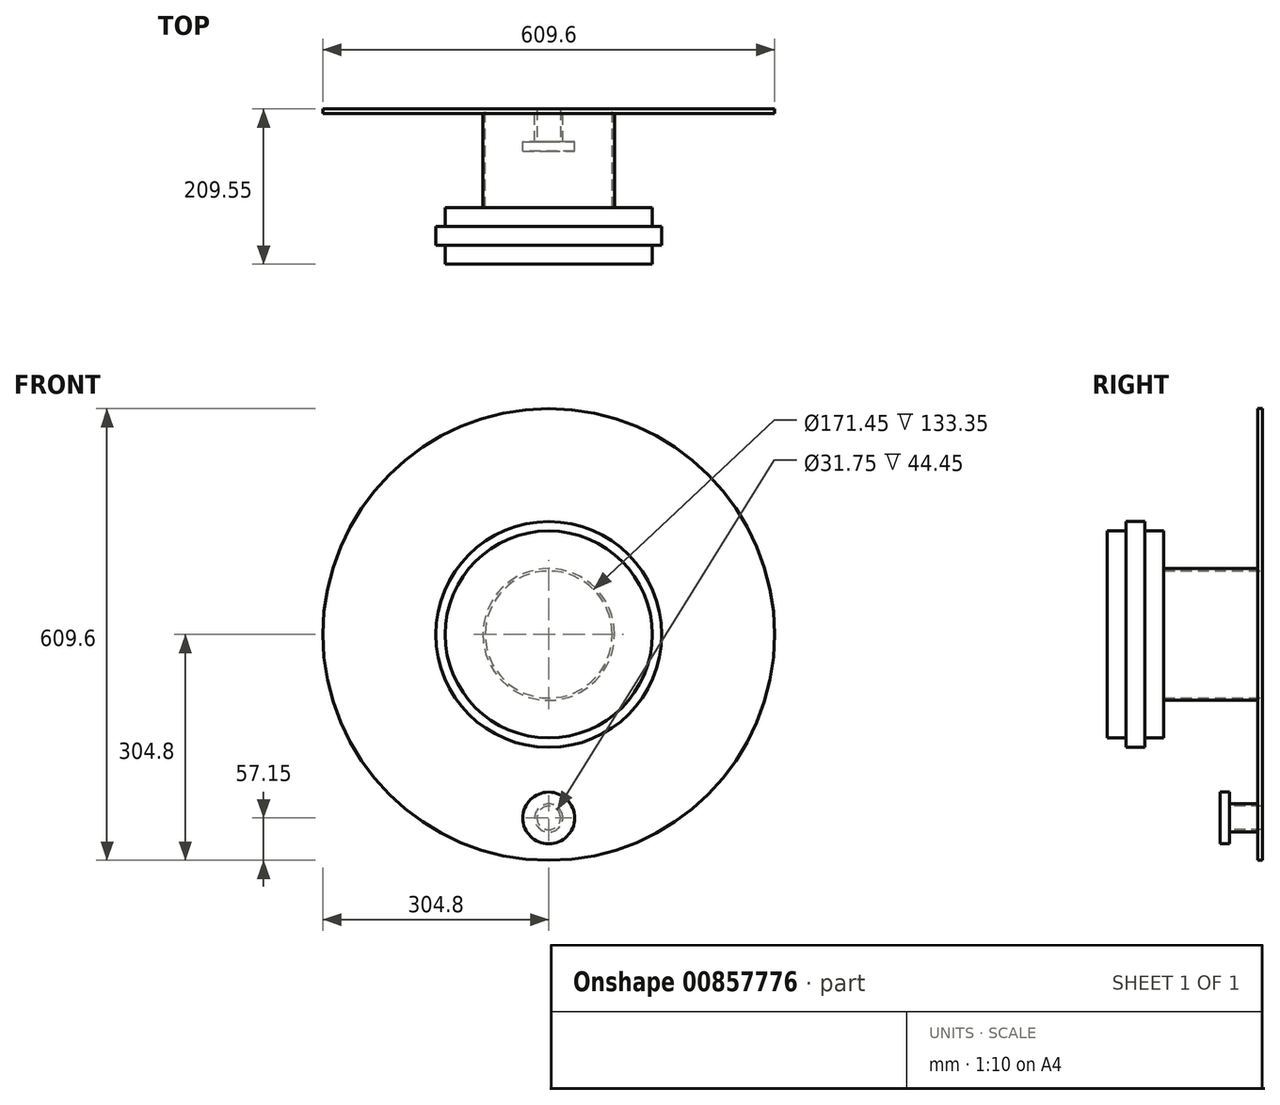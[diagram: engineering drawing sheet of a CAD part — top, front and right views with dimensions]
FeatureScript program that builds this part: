
annotation { "Feature Type Name" : "Feature", "Feature Type Description" : "" }
export const myFeature = defineFeature(function(context is Context, id is Id, definition is map)
    precondition{}
    {
        {
            var Q0;
            Q0=qCreatedBy(makeId("Front.planeOp"),FACE);
            var sketch = newSketch(context, id + "F0", { "sketchPlane" : qUnion([Q0])});
            skCircle(sketch, "E0", {"center": v(0, 0) * mm, "radius": 304.8 * mm});
            skSolve(sketch);
        }
        {
            var Q0;
            Q0=makeQuery(id+"F0.imprint","IMPRINT",FACE,{"disambiguationData":[TD([[makeQuery(id+"F0.imprint","IMPRINT",EDGE,{"derivedFrom":sQuery(id+"F0.wireOp",EDGE,"E0")}),1.0]])]});
            extrude(context, id + "F1", {"entities" : qUnion([Q0]), "depth" : 6.35 * mm});
        }
        {
            var Q0;
            Q0=makeQuery(id+"F1.opExtrude","CAP_FACE",FACE,{"disambiguationData":[OSD([sQuery(id+"F0.wireOp",EDGE,"E0")])],"isStart":false});
            var sketch = newSketch(context, id + "F2", { "sketchPlane" : qUnion([Q0])});
            skCircle(sketch, "E1", {"center": v(0, 0) * mm, "radius": 85.73 * mm});
            skCircle(sketch, "E2", {"center": v(0, 0) * mm, "radius": 88.9 * mm});
            skCircle(sketch, "E3", {"center": v(0, 0) * mm, "radius": 139.7 * mm});
            skCircle(sketch, "E4", {"center": v(0, 0) * mm, "radius": 152.4 * mm});
            skCircle(sketch, "E5", {"center": v(0, -247.65) * mm, "radius": 34.93 * mm});
            skLineSegment(sketch, "E6", {"start": v(0, 0) * mm, "end": v(0, -247.65) * mm, "construction": true});
            skCircle(sketch, "E7", {"center": v(0, -247.65) * mm, "radius": 19.05 * mm});
            skCircle(sketch, "E8", {"center": v(0, -247.65) * mm, "radius": 15.88 * mm});
            skSolve(sketch);
        }
        {
            var Q0;
            Q0=makeQuery(id+"F2.imprint","IMPRINT",FACE,{"disambiguationData":[TD([[makeQuery(id+"F2.imprint","IMPRINT",EDGE,{"derivedFrom":sQuery(id+"F2.wireOp",EDGE,"E1")}),-1.0]])]});
            extrude(context, id + "F3", {"entities" : qUnion([Q0]), "operationType" : NewBodyOperationType.ADD, "depth" : 127 * mm});
        }
        {
            var Q0;
            Q0=makeQuery(id+"F2.imprint","IMPRINT",FACE,{"disambiguationData":[TD([[makeQuery(id+"F2.imprint","IMPRINT",EDGE,{"derivedFrom":sQuery(id+"F2.wireOp",EDGE,"E1")}),1.0]])]});
            var Q1;
            Q1=sQuery(id+"F2.wireOp",EDGE,"E1");
            extrude(context, id + "F4", {"entities" : qUnion([Q0]), "operationType" : NewBodyOperationType.REMOVE, "surfaceEntities" : qUnion([Q1]), "oppositeDirection" : true, "depth" : 25.4 * mm});
        }
        {
            var Q0;
            Q0=makeQuery(id+"F2.imprint","IMPRINT",FACE,{"disambiguationData":[TD([[makeQuery(id+"F2.imprint","IMPRINT",EDGE,{"derivedFrom":sQuery(id+"F2.wireOp",EDGE,"E2")}),-1.0]])]});
            var Q1;
            Q1=makeQuery(id+"F2.imprint","IMPRINT",FACE,{"disambiguationData":[TD([[makeQuery(id+"F2.imprint","IMPRINT",EDGE,{"derivedFrom":sQuery(id+"F2.wireOp",EDGE,"E1")}),1.0]])]});
            var Q2;
            Q2=makeQuery(id+"F2.imprint","IMPRINT",FACE,{"disambiguationData":[TD([[makeQuery(id+"F2.imprint","IMPRINT",EDGE,{"derivedFrom":sQuery(id+"F2.wireOp",EDGE,"E1")}),-1.0]])]});
            extrude(context, id + "F5", {"entities" : qUnion([Q0, Q1, Q2]), "operationType" : NewBodyOperationType.ADD, "depth" : 152.4 * mm, "hasSecondDirection" : true, "secondDirectionOppositeDirection" : false, "secondDirectionDepth" : 127 * mm});
        }
        {
            var Q0;
            Q0=makeQuery(id+"F2.imprint","IMPRINT",FACE,{"disambiguationData":[TD([[makeQuery(id+"F2.imprint","IMPRINT",EDGE,{"derivedFrom":sQuery(id+"F2.wireOp",EDGE,"E3")}),-1.0]])]});
            var Q1;
            Q1=makeQuery(id+"F2.imprint","IMPRINT",FACE,{"disambiguationData":[TD([[makeQuery(id+"F2.imprint","IMPRINT",EDGE,{"derivedFrom":sQuery(id+"F2.wireOp",EDGE,"E2")}),-1.0]])]});
            var Q2;
            Q2=makeQuery(id+"F2.imprint","IMPRINT",FACE,{"disambiguationData":[TD([[makeQuery(id+"F2.imprint","IMPRINT",EDGE,{"derivedFrom":sQuery(id+"F2.wireOp",EDGE,"E1")}),-1.0]])]});
            var Q3;
            Q3=makeQuery(id+"F2.imprint","IMPRINT",FACE,{"disambiguationData":[TD([[makeQuery(id+"F2.imprint","IMPRINT",EDGE,{"derivedFrom":sQuery(id+"F2.wireOp",EDGE,"E1")}),1.0]])]});
            extrude(context, id + "F6", {"entities" : qUnion([Q0, Q1, Q2, Q3]), "operationType" : NewBodyOperationType.ADD, "depth" : 177.8 * mm, "hasSecondDirection" : true, "secondDirectionOppositeDirection" : false, "secondDirectionDepth" : 152.4 * mm});
        }
        {
            var Q0;
            Q0=makeQuery(id+"F2.imprint","IMPRINT",FACE,{"disambiguationData":[TD([[makeQuery(id+"F2.imprint","IMPRINT",EDGE,{"derivedFrom":sQuery(id+"F2.wireOp",EDGE,"E2")}),-1.0]])]});
            var Q1;
            Q1=makeQuery(id+"F2.imprint","IMPRINT",FACE,{"disambiguationData":[TD([[makeQuery(id+"F2.imprint","IMPRINT",EDGE,{"derivedFrom":sQuery(id+"F2.wireOp",EDGE,"E1")}),-1.0]])]});
            var Q2;
            Q2=makeQuery(id+"F2.imprint","IMPRINT",FACE,{"disambiguationData":[TD([[makeQuery(id+"F2.imprint","IMPRINT",EDGE,{"derivedFrom":sQuery(id+"F2.wireOp",EDGE,"E1")}),1.0]])]});
            extrude(context, id + "F7", {"entities" : qUnion([Q0, Q1, Q2]), "operationType" : NewBodyOperationType.ADD, "depth" : 203.2 * mm, "hasSecondDirection" : true, "secondDirectionOppositeDirection" : false, "secondDirectionDepth" : 177.8 * mm});
        }
        {
            var Q0;
            Q0=makeQuery(id+"F2.imprint","IMPRINT",FACE,{"disambiguationData":[TD([[makeQuery(id+"F2.imprint","IMPRINT",EDGE,{"derivedFrom":sQuery(id+"F2.wireOp",EDGE,"E8")}),1.0]])]});
            extrude(context, id + "F8", {"entities" : qUnion([Q0]), "operationType" : NewBodyOperationType.REMOVE, "oppositeDirection" : true, "depth" : 25.4 * mm});
        }
        {
            var Q0;
            Q0=makeQuery(id+"F2.imprint","IMPRINT",FACE,{"disambiguationData":[TD([[makeQuery(id+"F2.imprint","IMPRINT",EDGE,{"derivedFrom":sQuery(id+"F2.wireOp",EDGE,"E7")}),1.0]])]});
            extrude(context, id + "F9", {"entities" : qUnion([Q0]), "operationType" : NewBodyOperationType.ADD, "depth" : 38.1 * mm});
        }
        {
            var Q0;
            Q0=makeQuery(id+"F2.imprint","IMPRINT",FACE,{"disambiguationData":[TD([[makeQuery(id+"F2.imprint","IMPRINT",EDGE,{"derivedFrom":sQuery(id+"F2.wireOp",EDGE,"E5")}),1.0]])]});
            var Q1;
            Q1=makeQuery(id+"F2.imprint","IMPRINT",FACE,{"disambiguationData":[TD([[makeQuery(id+"F2.imprint","IMPRINT",EDGE,{"derivedFrom":sQuery(id+"F2.wireOp",EDGE,"E7")}),1.0]])]});
            var Q2;
            Q2=makeQuery(id+"F2.imprint","IMPRINT",FACE,{"disambiguationData":[TD([[makeQuery(id+"F2.imprint","IMPRINT",EDGE,{"derivedFrom":sQuery(id+"F2.wireOp",EDGE,"E8")}),1.0]])]});
            extrude(context, id + "F10", {"entities" : qUnion([Q0, Q1, Q2]), "operationType" : NewBodyOperationType.ADD, "depth" : 50.8 * mm, "hasSecondDirection" : true, "secondDirectionOppositeDirection" : false, "secondDirectionDepth" : 38.1 * mm});
        }
    });
